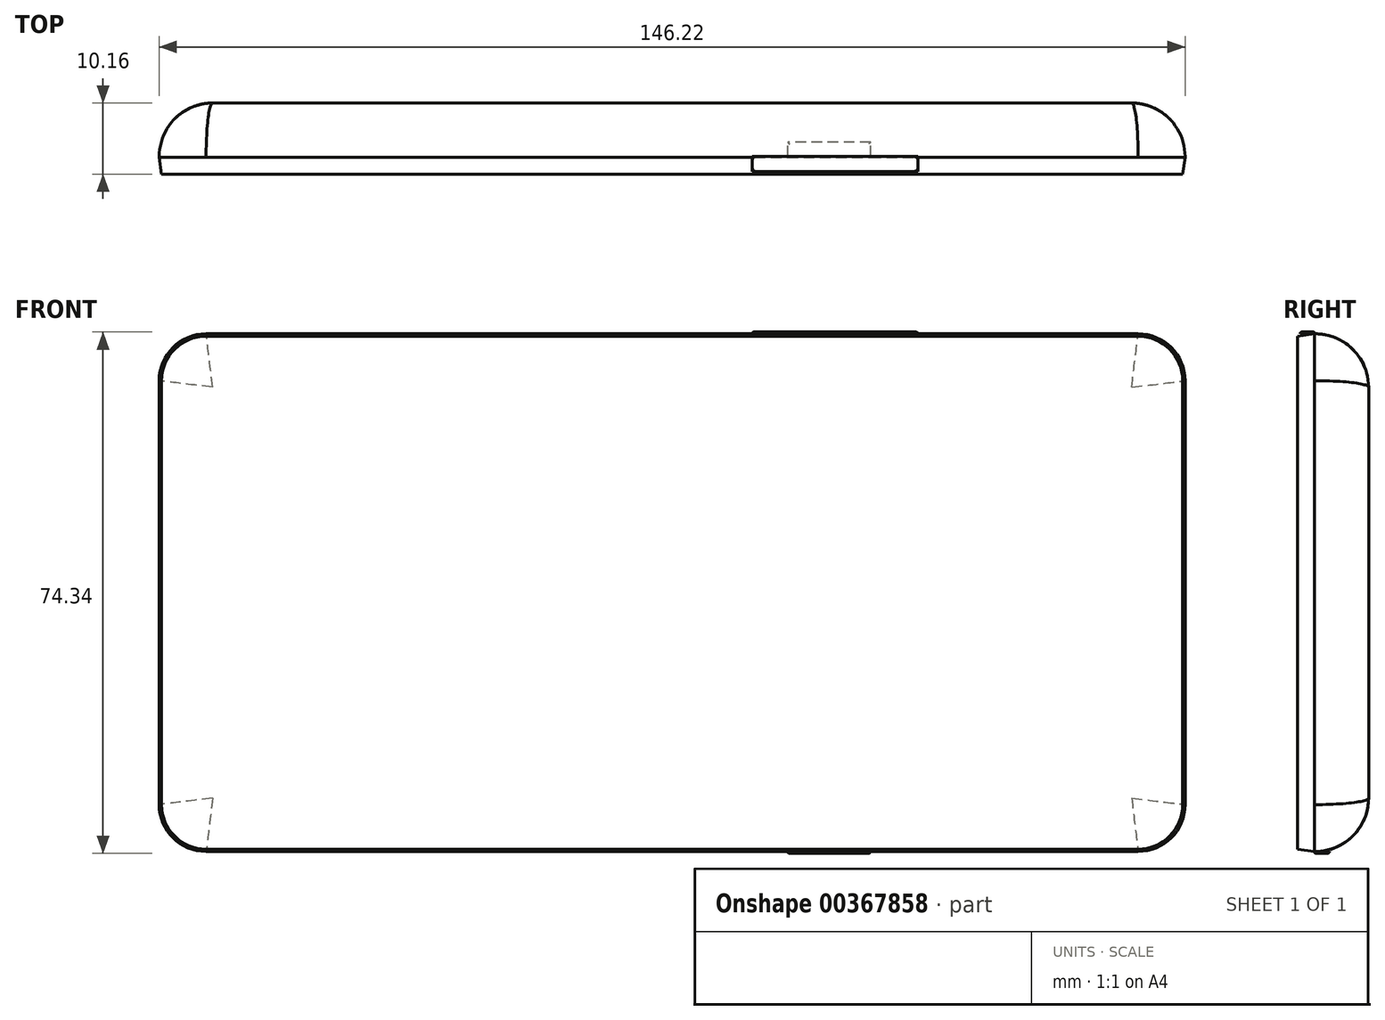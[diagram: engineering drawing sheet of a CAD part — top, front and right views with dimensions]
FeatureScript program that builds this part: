
annotation { "Feature Type Name" : "Feature", "Feature Type Description" : "" }
export const myFeature = defineFeature(function(context is Context, id is Id, definition is map)
    precondition{}
    {
        {
            var Q0;
            Q0=qCreatedBy(makeId("Front.planeOp"),FACE);
            var sketch = newSketch(context, id + "F0", { "sketchPlane" : qUnion([Q0])});
            skLineSegment(sketch, "E0.bottom", {"start": v(66.42, 36.58) * mm, "end": v(-66.42, 36.58) * mm});
            skLineSegment(sketch, "E0.top", {"start": v(66.42, -36.58) * mm, "end": v(-66.42, -36.58) * mm});
            skLineSegment(sketch, "E0.left", {"start": v(72.77, 30.23) * mm, "end": v(72.77, -30.23) * mm});
            skLineSegment(sketch, "E0.right", {"start": v(-72.77, 30.23) * mm, "end": v(-72.77, -30.23) * mm});
            skPoint(sketch, "E0.middle", {"position": v(0, 0) * mm});
            skPoint(sketch, "E1.visualSharp", {"position": v(-72.77, 36.58) * mm});
            skArc(sketch, "E1.filletArc", {"start": v(-66.42, 36.58) * mm, "mid": v(-70.91, 34.72) * mm, "end": v(-72.77, 30.23) * mm});
            skPoint(sketch, "E2.visualSharp", {"position": v(-72.77, -36.58) * mm});
            skArc(sketch, "E2.filletArc", {"start": v(-72.77, -30.23) * mm, "mid": v(-70.91, -34.72) * mm, "end": v(-66.42, -36.58) * mm});
            skPoint(sketch, "E3.visualSharp", {"position": v(72.77, 36.58) * mm});
            skArc(sketch, "E3.filletArc", {"start": v(72.77, 30.23) * mm, "mid": v(70.91, 34.72) * mm, "end": v(66.42, 36.58) * mm});
            skPoint(sketch, "E4.visualSharp", {"position": v(72.77, -36.58) * mm});
            skArc(sketch, "E4.filletArc", {"start": v(66.42, -36.58) * mm, "mid": v(70.91, -34.72) * mm, "end": v(72.77, -30.23) * mm});
            skSolve(sketch);
        }
        {
            var Q0;
            Q0=makeQuery(id+"F0.imprint","IMPRINT",FACE,{"disambiguationData":[TD([[makeQuery(id+"F0.imprint","IMPRINT",EDGE,{"derivedFrom":sQuery(id+"F0.wireOp",EDGE,"E0.bottom")}),1.0]])]});
            extrude(context, id + "F1", {"entities" : qUnion([Q0]), "oppositeDirection" : true, "depth" : 2.41 * mm, "hasDraft" : true, "draftAngle" : 8 * degree});
        }
        {
            var Q0;
            Q0=makeQuery(id+"F1.opExtrude","CAP_FACE",FACE,{"disambiguationData":[OSD([sQuery(id+"F0.wireOp",EDGE,"E0.bottom"),sQuery(id+"F0.wireOp",EDGE,"E0.top"),sQuery(id+"F0.wireOp",EDGE,"E0.left"),sQuery(id+"F0.wireOp",EDGE,"E0.right"),sQuery(id+"F0.wireOp",EDGE,"E1.filletArc"),sQuery(id+"F0.wireOp",EDGE,"E2.filletArc"),sQuery(id+"F0.wireOp",EDGE,"E3.filletArc"),sQuery(id+"F0.wireOp",EDGE,"E4.filletArc")])],"isStart":false});
            var sketch = newSketch(context, id + "F2", { "sketchPlane" : qUnion([Q0])});
            skSolve(sketch);
        }
        {
            var Q0;
            Q0 = qSketchRegion(id + "F2", true);
            var Q1;
            Q1=makeQuery(id+"F2.imprint","IMPRINT",FACE,{"disambiguationData":[TD([[makeQuery(id+"F2.imprint","IMPRINT",EDGE,{"derivedFrom":makeQuery(id+"F1.opExtrude","CAP_EDGE",EDGE,{"disambiguationData":[OSD([sQuery(id+"F0.wireOp",EDGE,"E0.bottom")])],"isStart":false})}),-1.0]])]});
            extrude(context, id + "F3", {"entities" : qUnion([Q0, Q1]), "operationType" : NewBodyOperationType.ADD, "depth" : 2.16 * mm});
        }
        {
            var Q0;
            Q0=makeQuery(id+"F3.opExtrude","CAP_FACE",FACE,{"disambiguationData":[OSD([sQuery(id+"F0.wireOp",EDGE,"E0.bottom"),sQuery(id+"F0.wireOp",EDGE,"E0.top"),sQuery(id+"F0.wireOp",EDGE,"E0.left"),sQuery(id+"F0.wireOp",EDGE,"E0.right"),sQuery(id+"F0.wireOp",EDGE,"E1.filletArc"),sQuery(id+"F0.wireOp",EDGE,"E2.filletArc"),sQuery(id+"F0.wireOp",EDGE,"E3.filletArc"),sQuery(id+"F0.wireOp",EDGE,"E4.filletArc")])],"isStart":false});
            var sketch = newSketch(context, id + "F4", { "sketchPlane" : qUnion([Q0])});
            skSolve(sketch);
        }
        {
            var Q0;
            Q0 = qSketchRegion(id + "F4", true);
            var Q1;
            Q1=makeQuery(id+"F4.imprint","IMPRINT",FACE,{"disambiguationData":[TD([[makeQuery(id+"F4.imprint","IMPRINT",EDGE,{"derivedFrom":makeQuery(id+"F3.opExtrude","CAP_EDGE",EDGE,{"disambiguationData":[OSD([sQuery(id+"F0.wireOp",EDGE,"E0.bottom")])],"isStart":false})}),-1.0]])]});
            extrude(context, id + "F5", {"entities" : qUnion([Q0, Q1]), "operationType" : NewBodyOperationType.ADD, "depth" : 5.6 * mm});
        }
        {
            var Q0;
            Q0=makeQuery(id+"F5.opExtrude","CAP_FACE",FACE,{"disambiguationData":[OSD([sQuery(id+"F0.wireOp",EDGE,"E0.bottom"),sQuery(id+"F0.wireOp",EDGE,"E0.top"),sQuery(id+"F0.wireOp",EDGE,"E0.left"),sQuery(id+"F0.wireOp",EDGE,"E0.right"),sQuery(id+"F0.wireOp",EDGE,"E1.filletArc"),sQuery(id+"F0.wireOp",EDGE,"E2.filletArc"),sQuery(id+"F0.wireOp",EDGE,"E3.filletArc"),sQuery(id+"F0.wireOp",EDGE,"E4.filletArc")])],"isStart":false});
            fillet(context, id + "F6", {"entities" : qUnion([Q0]), "radius" : 7.62 * mm, "tangentPropagation" : true, "allowEdgeOverflow" : false});
        }
        {
            var Q0;
            {var subQ0=sQuery(id+"F0.wireOp",EDGE,"E0.top");Q0=makeQuery(id+"F5.boolean.opBoolean","MERGE",FACE,{"derivedFrom":[makeQuery(id+"F3.opExtrude","SWEPT_FACE",FACE,{"disambiguationData":[OSD([subQ0])]}),makeQuery(id+"F5.opExtrude","SWEPT_FACE",FACE,{"disambiguationData":[OSD([subQ0])]})]});}
            var sketch = newSketch(context, id + "F7", { "sketchPlane" : qUnion([Q0])});
            skLineSegment(sketch, "E5.bottom", {"start": v(28.28, -2.41) * mm, "end": v(16.47, -2.41) * mm});
            skLineSegment(sketch, "E5.top", {"start": v(28.28, -4.57) * mm, "end": v(16.47, -4.57) * mm});
            skLineSegment(sketch, "E5.left", {"start": v(28.28, -2.41) * mm, "end": v(28.28, -4.57) * mm});
            skLineSegment(sketch, "E5.right", {"start": v(16.47, -2.41) * mm, "end": v(16.47, -4.57) * mm});
            skPoint(sketch, "E5.middle", {"position": v(22.37, -3.5) * mm});
            skSolve(sketch);
        }
        {
            var Q0;
            Q0 = qSketchRegion(id + "F7", true);
            extrude(context, id + "F8", {"entities" : qUnion([Q0]), "operationType" : NewBodyOperationType.ADD, "depth" : 0.25 * mm});
        }
        {
            var Q0;
            Q0=makeQuery(id+"F8.opExtrude","CAP_FACE",FACE,{"disambiguationData":[OSD([sQuery(id+"F7.wireOp",EDGE,"E5.bottom"),sQuery(id+"F7.wireOp",EDGE,"E5.top"),sQuery(id+"F7.wireOp",EDGE,"E5.left"),sQuery(id+"F7.wireOp",EDGE,"E5.right")])],"isStart":false});
            fillet(context, id + "F9", {"entities" : qUnion([Q0]), "radius" : 0.25 * mm, "tangentPropagation" : true, "allowEdgeOverflow" : false});
        }
        {
            var Q0;
            {var subQ0=sQuery(id+"F0.wireOp",EDGE,"E0.bottom");Q0=makeQuery(id+"F5.boolean.opBoolean","MERGE",FACE,{"derivedFrom":[makeQuery(id+"F3.opExtrude","SWEPT_FACE",FACE,{"disambiguationData":[OSD([subQ0])]}),makeQuery(id+"F5.opExtrude","SWEPT_FACE",FACE,{"disambiguationData":[OSD([subQ0])]})]});}
            var sketch = newSketch(context, id + "F10", { "sketchPlane" : qUnion([Q0])});
            skLineSegment(sketch, "E6.bottom", {"start": v(23.2, 2.54) * mm, "end": v(35.01, 2.54) * mm});
            skLineSegment(sketch, "E6.top", {"start": v(23.2, 0.38) * mm, "end": v(35.01, 0.38) * mm});
            skLineSegment(sketch, "E6.left", {"start": v(23.2, 2.54) * mm, "end": v(23.2, 0.38) * mm});
            skLineSegment(sketch, "E6.right", {"start": v(35.01, 2.54) * mm, "end": v(35.01, 0.38) * mm});
            skLineSegment(sketch, "E7.bottom", {"start": v(23.2, 0.38) * mm, "end": v(11.39, 0.38) * mm});
            skLineSegment(sketch, "E7.top", {"start": v(23.2, 2.54) * mm, "end": v(11.39, 2.54) * mm});
            skLineSegment(sketch, "E7.left", {"start": v(23.2, 0.38) * mm, "end": v(23.2, 2.54) * mm});
            skLineSegment(sketch, "E7.right", {"start": v(11.39, 0.38) * mm, "end": v(11.39, 2.54) * mm});
            skSolve(sketch);
        }
        {
            var Q0;
            Q0 = qSketchRegion(id + "F10", true);
            extrude(context, id + "F11", {"entities" : qUnion([Q0]), "operationType" : NewBodyOperationType.ADD, "depth" : 0.25 * mm});
        }
        {
            var Q0;
            Q0=makeQuery(id+"F11.opExtrude","CAP_FACE",FACE,{"disambiguationData":[OSD([sQuery(id+"F10.wireOp",EDGE,"E6.bottom"),sQuery(id+"F10.wireOp",EDGE,"E6.top"),sQuery(id+"F10.wireOp",EDGE,"E6.right"),sQuery(id+"F10.wireOp",EDGE,"E7.bottom"),sQuery(id+"F10.wireOp",EDGE,"E7.top"),sQuery(id+"F10.wireOp",EDGE,"E7.right")])],"isStart":false});
            fillet(context, id + "F12", {"entities" : qUnion([Q0]), "radius" : 0.25 * mm, "tangentPropagation" : true, "allowEdgeOverflow" : false});
        }
    });
